# Revit family: Maxlogic Akıllı adresli duman damper modülü ( Tekli )
name_source: partatom
category: Fire Alarm Devices
units: mm (PartAtom-declared; Revit-internal decimal feet)

## family parameters
Cut with Voids When Loaded = No
Host = Face
Maintain Annotation Orientation = Yes
OmniClass Number = 23.85.30.21
OmniClass Title = Environmental Detection/Registration
Part Type = Normal
Room Calculation Point = No
Round Connector Dimension = Use Diameter
Shared = No

## types (6) — shared parameters
Code Performance = EN 54-17 / EN 54-18
Color = Beyaz
Device Adress Setup = El tipi adresleme cihazı
Fax Number = (+)90 216 466 45 10
Installation Manual = https://mavilielektronik.com
Main Material = White Plastic ABS
Manufacturer = Mavili Elektronik Ticaret A.Ş.
Model = Maxlogic
Mounting surface = Duvara montaj
Nominal Depth = 60 mm
Nominal Height = 86 mm
Nominal Wıdth = 158 mm
Operating temperature = (-30°C) - (+60°C)
Operating voltage range = 18-33V/DC
Operatonal Voltage (default) = 24 V/DC
Secondary Material = Plastic
URL = https://www.mavili.com.tr
Warranty Duration Labor = 2
Warranty Duration Parts = 2
Warranty Duration Unit = Year
zero-valued in all types: Cost, Default Elevation

## per-type parameters (varying)
| type | Description | External supply | Product Code |
| Maxlogic akıllı adresli duman damper modülü 24V DC | Akıllı adresli duman damper modülü 24V DC | 24 V/DC | ML-1356 |
| Maxlogic akıllı adresli duman damper modülü 24V DC Kısa devre izolatörlü | Akıllı adresli duman damper modülü 24V DC Kısa devre izolatörlü | 24 V/DC | ML-1356.SCI |
| Maxlogic akıllı adresli duman damper modülü 24V AC | Akıllı adresli duman damper modülü 24V AC | 24 V/AC | ML-1357 |
| Maxlogic akıllı adresli duman damper modülü 24V AC Kısa devre izolatörlü | Akıllı adresli duman damper modülü 24V AC Kısa devre izolatörlü | 24 V/AC | ML-1357.SCI |
| Maxlogic akıllı adresli duman damper modülü 220V AC | Akıllı adresli duman damper modülü 220V AC | 220 V/AC | ML-1358 |
| Maxlogic akıllı adresli duman damper modülü 220V AC Kısa devre izolatörlü | Akıllı adresli duman damper modülü 220V AC Kısa devre izolatörlü | 220 V/AC | ML-1358.SCI |

## geometry (parser evidence)
native form markers: Sweep x2
no freeform markers — native parametric forms only
